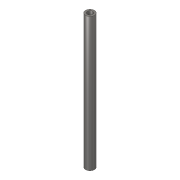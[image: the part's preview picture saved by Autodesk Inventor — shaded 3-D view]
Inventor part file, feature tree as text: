
AUTODESK INVENTOR PART (.ipt)
format: ipt  version: 2018 (Build 220112000, 112)  size: 74,752 bytes
history: native  units: mm
features: extrude x1, sketch x1
ambient origin geometry x8: Origin, YZ Plane, XZ Plane, XY Plane, X Axis, Y Axis, Z Axis, Center Point
bodies: Solid1 (feature_tree)
feature tree (2):
  extrude  "Extrusion1"  Depth=300.0mm
  sketch  "Sketch1"  dims[d0=20.0mm d2=4.0mm d3=300.0mm d4=0.0mm]
